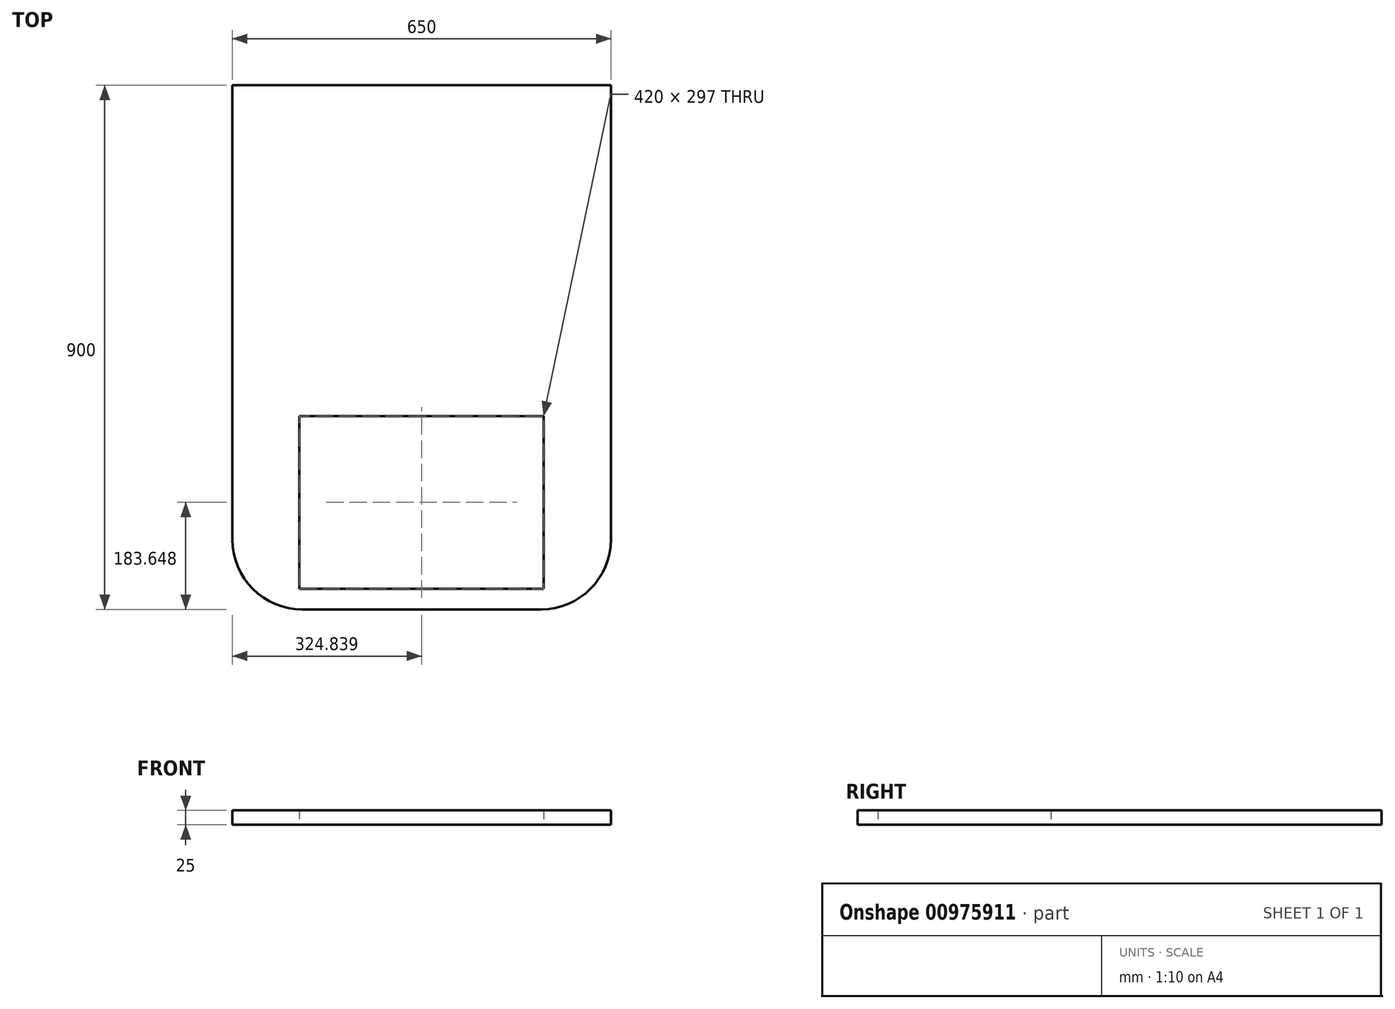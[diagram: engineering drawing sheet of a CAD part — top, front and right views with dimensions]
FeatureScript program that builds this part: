
annotation { "Feature Type Name" : "Feature", "Feature Type Description" : "" }
export const myFeature = defineFeature(function(context is Context, id is Id, definition is map)
    precondition{}
    {
        {
            var Q0;
            Q0=qCreatedBy(makeId("Top.planeOp"),FACE);
            var sketch = newSketch(context, id + "F0", { "sketchPlane" : qUnion([Q0])});
            skLineSegment(sketch, "E0.bottom", {"start": v(-613.33, 748.9) * mm, "end": v(36.67, 748.9) * mm});
            skLineSegment(sketch, "E0.top", {"start": v(-493.33, -151.1) * mm, "end": v(-83.33, -151.1) * mm});
            skLineSegment(sketch, "E0.left", {"start": v(-613.33, 748.9) * mm, "end": v(-613.33, -31.1) * mm});
            skLineSegment(sketch, "E0.right", {"start": v(36.67, 748.9) * mm, "end": v(36.67, -31.1) * mm});
            skPoint(sketch, "E1.visualSharp", {"position": v(-613.33, -151.1) * mm});
            skArc(sketch, "E1.filletArc", {"start": v(-613.33, -31.1) * mm, "mid": v(-578.18, -115.96) * mm, "end": v(-493.33, -151.1) * mm});
            skPoint(sketch, "E2.visualSharp", {"position": v(36.67, -151.1) * mm});
            skArc(sketch, "E2.filletArc", {"start": v(-83.33, -151.1) * mm, "mid": v(1.52, -115.96) * mm, "end": v(36.67, -31.1) * mm});
            skPoint(sketch, "E3.firstSnap0", {"position": v(-578.18, -115.96) * mm});
            skLineSegment(sketch, "E3.bottom", {"start": v(-498.5, -115.96) * mm, "end": v(-78.5, -115.96) * mm});
            skLineSegment(sketch, "E3.top", {"start": v(-498.5, 181.04) * mm, "end": v(-78.5, 181.04) * mm});
            skLineSegment(sketch, "E3.left", {"start": v(-498.5, -115.96) * mm, "end": v(-498.5, 181.04) * mm});
            skLineSegment(sketch, "E3.right", {"start": v(-78.5, -115.96) * mm, "end": v(-78.5, 181.04) * mm});
            skSolve(sketch);
        }
        {
            var Q0;
            Q0=makeQuery(id+"F0.imprint","IMPRINT",FACE,{"disambiguationData":[TD([[makeQuery(id+"F0.imprint","IMPRINT",EDGE,{"derivedFrom":sQuery(id+"F0.wireOp",EDGE,"E0.bottom")}),-1.0]])]});
            extrude(context, id + "F1", {"entities" : qUnion([Q0]), "depth" : 18 * mm, "offsetDistance" : 25 * mm});
        }
        {
            var Q0;
            Q0 = qSketchRegion(id + "F0", true);
            extrude(context, id + "F2", {"entities" : qUnion([Q0]), "operationType" : NewBodyOperationType.ADD, "depth" : 25 * mm, "offsetDistance" : 25 * mm});
        }
    });
